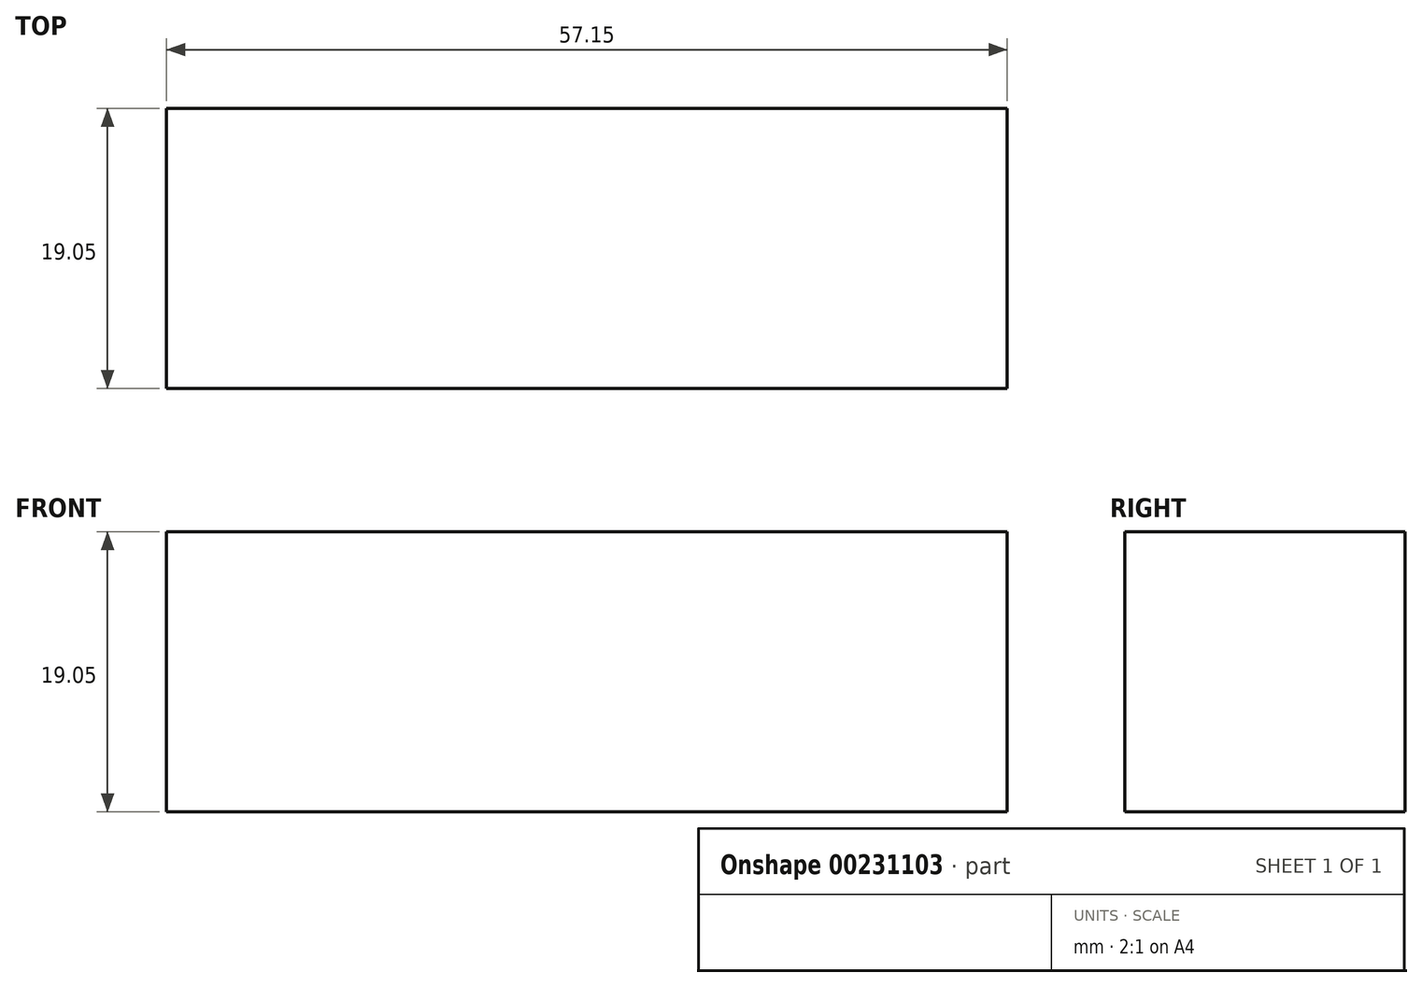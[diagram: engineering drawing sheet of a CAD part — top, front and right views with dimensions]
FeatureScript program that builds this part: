
annotation { "Feature Type Name" : "Feature", "Feature Type Description" : "" }
export const myFeature = defineFeature(function(context is Context, id is Id, definition is map)
    precondition{}
    {
        {
            var Q0;
            Q0=qCreatedBy(makeId("Front.planeOp"),FACE);
            var sketch = newSketch(context, id + "F0", { "sketchPlane" : qUnion([Q0])});
            skLineSegment(sketch, "E0.bottom", {"start": v(-47.63, 31.55) * mm, "end": v(9.52, 31.55) * mm});
            skLineSegment(sketch, "E0.top", {"start": v(-47.63, 12.5) * mm, "end": v(9.52, 12.5) * mm});
            skLineSegment(sketch, "E0.left", {"start": v(-47.63, 31.55) * mm, "end": v(-47.63, 12.5) * mm});
            skLineSegment(sketch, "E0.right", {"start": v(9.52, 31.55) * mm, "end": v(9.52, 12.5) * mm});
            skLineSegment(sketch, "E1.bottom", {"start": v(-47.63, 31.55) * mm, "end": v(-28.58, 31.55) * mm});
            skLineSegment(sketch, "E1.top", {"start": v(-47.63, 50.6) * mm, "end": v(-28.58, 50.6) * mm});
            skLineSegment(sketch, "E1.left", {"start": v(-47.63, 31.55) * mm, "end": v(-47.63, 50.6) * mm});
            skLineSegment(sketch, "E1.right", {"start": v(-28.58, 31.55) * mm, "end": v(-28.58, 50.6) * mm});
            skLineSegment(sketch, "E2.bottom", {"start": v(9.52, 31.55) * mm, "end": v(-9.53, 31.55) * mm});
            skLineSegment(sketch, "E2.top", {"start": v(9.52, 50.6) * mm, "end": v(-9.53, 50.6) * mm});
            skLineSegment(sketch, "E2.left", {"start": v(9.52, 31.55) * mm, "end": v(9.52, 50.6) * mm});
            skLineSegment(sketch, "E2.right", {"start": v(-9.53, 31.55) * mm, "end": v(-9.53, 50.6) * mm});
            skSolve(sketch);
        }
        {
            var Q0;
            Q0=makeQuery(id+"F0.imprint","IMPRINT",FACE,{"disambiguationData":[TD([[makeQuery(id+"F0.imprint","IMPRINT",EDGE,{"derivedFrom":sQuery(id+"F0.wireOp",EDGE,"E2.bottom")}),-1.0]])]});
            var Q1;
            Q1=makeQuery(id+"F0.imprint","IMPRINT",FACE,{"disambiguationData":[TD([[makeQuery(id+"F0.imprint","IMPRINT",EDGE,{"derivedFrom":sQuery(id+"F0.wireOp",EDGE,"E0.bottom")}),-1.0]])]});
            var Q2;
            Q2=makeQuery(id+"F0.imprint","IMPRINT",FACE,{"disambiguationData":[TD([[makeQuery(id+"F0.imprint","IMPRINT",EDGE,{"derivedFrom":sQuery(id+"F0.wireOp",EDGE,"E1.bottom")}),1.0]])]});
            extrude(context, id + "F1", {"entities" : qUnion([Q0, Q1, Q2]), "depth" : 19.05 * mm});
        }
    });
